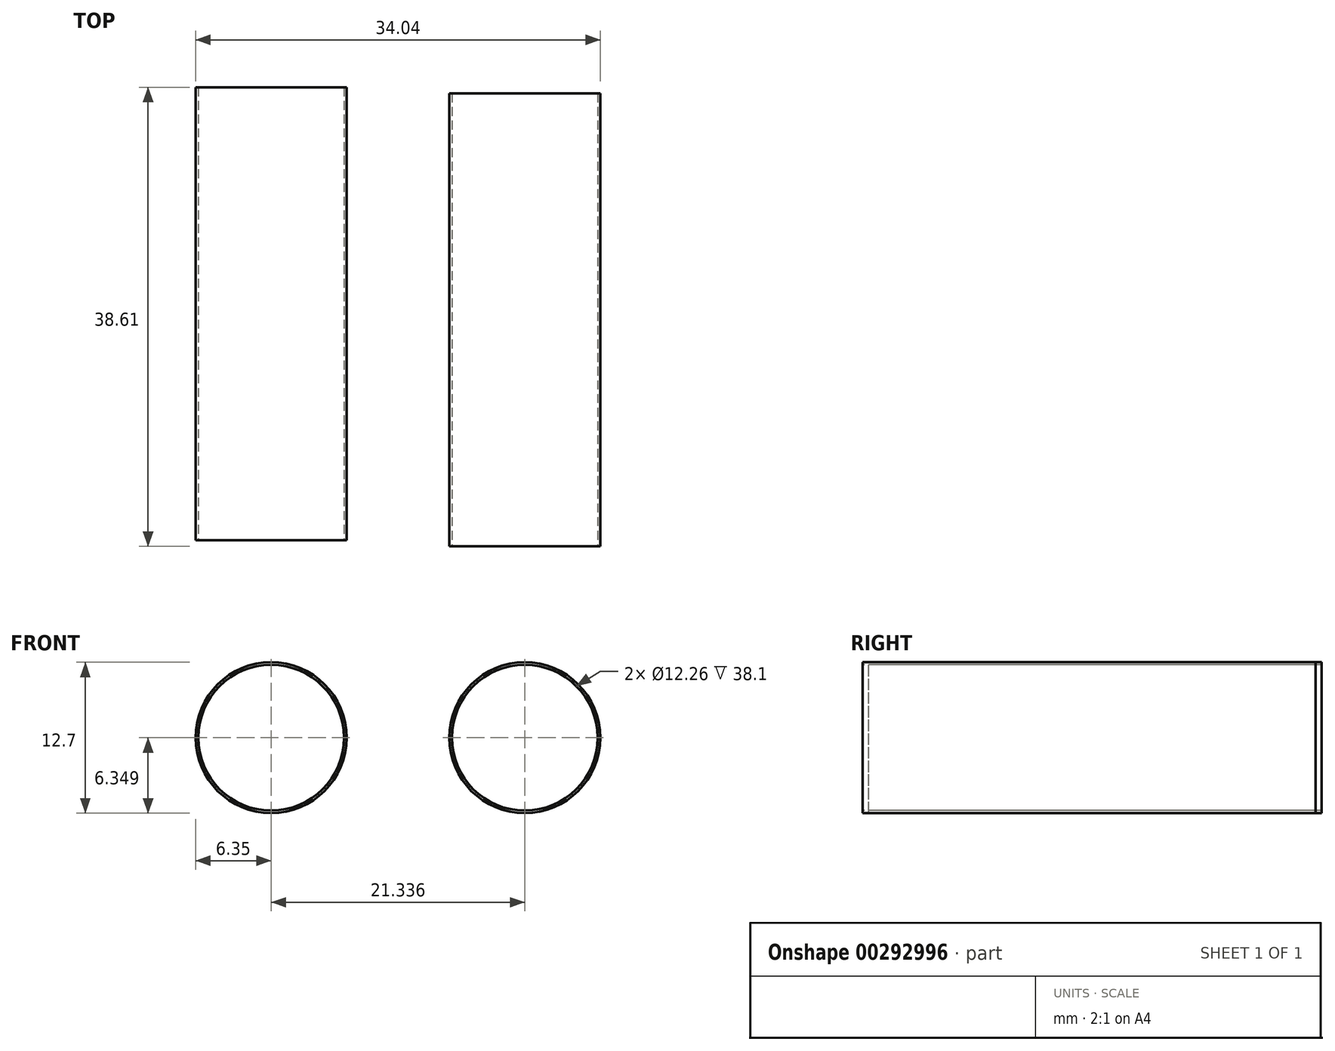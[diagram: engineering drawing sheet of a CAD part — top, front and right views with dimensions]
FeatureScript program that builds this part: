
annotation { "Feature Type Name" : "Feature", "Feature Type Description" : "" }
export const myFeature = defineFeature(function(context is Context, id is Id, definition is map)
    precondition{}
    {
        {
            var Q0;
            Q0=qCreatedBy(makeId("Front.planeOp"),FACE);
            var sketch = newSketch(context, id + "F0", { "sketchPlane" : qUnion([Q0])});
            skCircle(sketch, "E0", {"center": v(-53.53, -17) * mm, "radius": 6.35 * mm});
            skSolve(sketch);
        }
        {
            var Q0;
            Q0=makeQuery(id+"F0.imprint","IMPRINT",FACE,{"disambiguationData":[TD([[makeQuery(id+"F0.imprint","IMPRINT",EDGE,{"derivedFrom":sQuery(id+"F0.wireOp",EDGE,"E0")}),1.0]])]});
            extrude(context, id + "F1", {"entities" : qUnion([Q0]), "depth" : 38.1 * mm});
        }
        {
            var Q0;
            Q0=makeQuery(id+"F1.opExtrude","CAP_FACE",FACE,{"disambiguationData":[OSD([sQuery(id+"F0.wireOp",EDGE,"E0")])],"isStart":false});
            var sketch = newSketch(context, id + "F2", { "sketchPlane" : qUnion([Q0])});
            skCircle(sketch, "E1", {"center": v(-53.53, -17) * mm, "radius": 6.13 * mm});
            skSolve(sketch);
        }
        {
            var Q0;
            Q0 = qSketchRegion(id + "F2", true);
            extrude(context, id + "F3", {"entities" : qUnion([Q0]), "operationType" : NewBodyOperationType.REMOVE, "oppositeDirection" : true, "depth" : 38.1 * mm});
        }
        {
            var Q0;
            Q0=makeQuery(id+"F1.opExtrude","SWEPT_BODY",BODY,{"disambiguationData":[OSD([sQuery(id+"F0.wireOp",EDGE,"E0")])]});
            transform(context, id + "F4", {"entities" : qUnion([Q0]), "transformType" : TransformType.TRANSLATION_3D, "dx" : 21.34 * mm, "dy" : -0.5 * mm, "dz" : 0 * mm, "makeCopy" : true});
        }
    });
